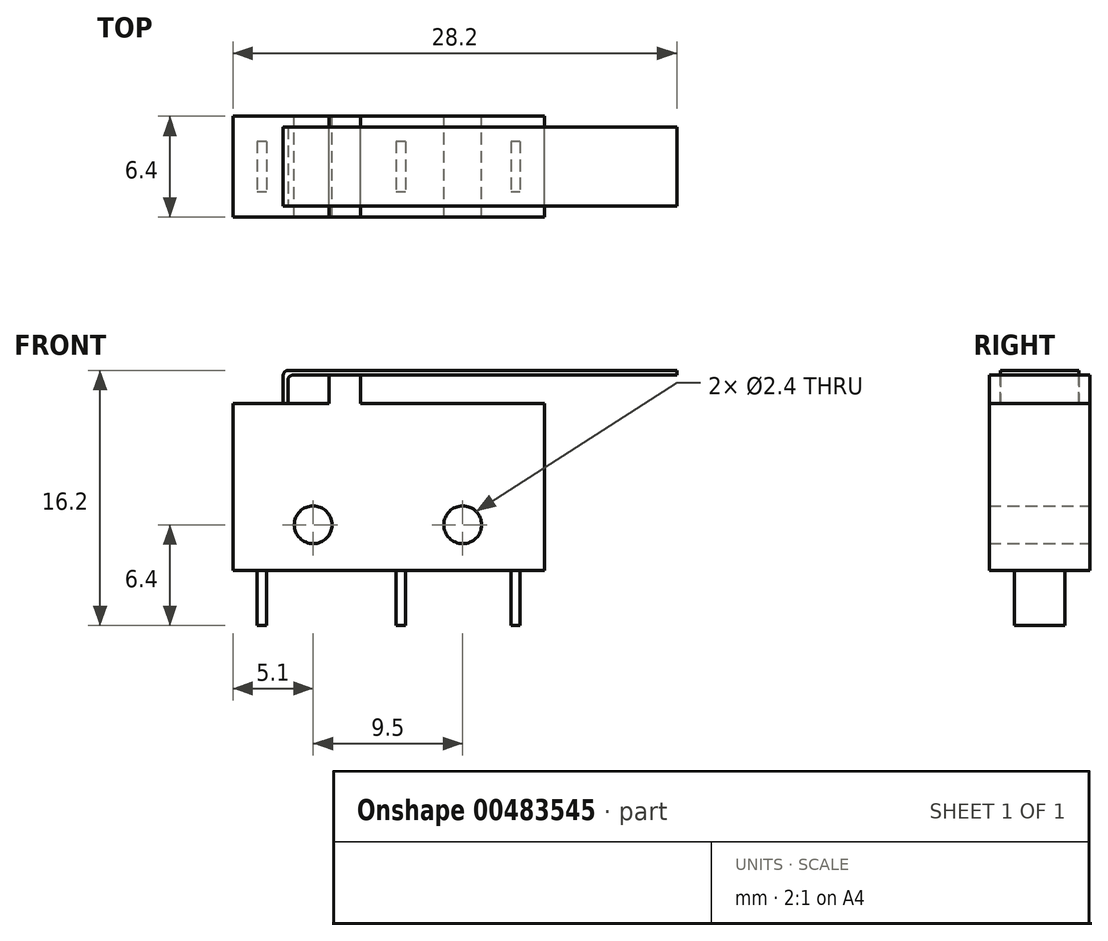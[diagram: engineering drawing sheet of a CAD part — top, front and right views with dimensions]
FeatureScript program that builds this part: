
annotation { "Feature Type Name" : "Feature", "Feature Type Description" : "" }
export const myFeature = defineFeature(function(context is Context, id is Id, definition is map)
    precondition{}
    {
        {
            var Q0;
            Q0=qCreatedBy(makeId("Front.planeOp"),FACE);
            var sketch = newSketch(context, id + "F0", { "sketchPlane" : qUnion([Q0])});
            skLineSegment(sketch, "E0.bottom", {"start": v(0, 0) * mm, "end": v(19.8, 0) * mm});
            skLineSegment(sketch, "E0.top", {"start": v(0, 10.6) * mm, "end": v(6.1, 10.6) * mm});
            skLineSegment(sketch, "E0.left", {"start": v(0, 0) * mm, "end": v(0, 10.6) * mm});
            skLineSegment(sketch, "E0.right", {"start": v(19.8, 0) * mm, "end": v(19.8, 10.6) * mm});
            skCircle(sketch, "E1", {"center": v(5.1, 2.9) * mm, "radius": 1.2 * mm});
            skCircle(sketch, "E2", {"center": v(14.6, 2.9) * mm, "radius": 1.2 * mm});
            skLineSegment(sketch, "E3", {"start": v(6.1, 10.6) * mm, "end": v(6.1, 12.4) * mm});
            skLineSegment(sketch, "E4", {"start": v(6.1, 12.4) * mm, "end": v(8.1, 12.4) * mm});
            skLineSegment(sketch, "E5", {"start": v(8.1, 12.4) * mm, "end": v(8.1, 10.6) * mm});
            skLineSegment(sketch, "E6.trimOffspring", {"start": v(8.1, 10.6) * mm, "end": v(19.8, 10.6) * mm});
            skSolve(sketch);
        }
        {
            var Q0;
            Q0 = qSketchRegion(id + "F0", true);
            extrude(context, id + "F1", {"entities" : qUnion([Q0]), "depth" : 6.4 * mm, "offsetDistance" : 25 * mm});
        }
        {
            var Q0;
            Q0=makeQuery(id+"F1.opExtrude","SWEPT_FACE",FACE,{"disambiguationData":[OSD([sQuery(id+"F0.wireOp",EDGE,"E0.bottom")])]});
            var sketch = newSketch(context, id + "F2", { "sketchPlane" : qUnion([Q0])});
            skLineSegment(sketch, "E7", {"start": v(0, 3.2) * mm, "end": v(19.8, 3.2) * mm, "construction": true});
            skLineSegment(sketch, "E8.bottom", {"start": v(2.15, 1.6) * mm, "end": v(1.55, 1.6) * mm});
            skLineSegment(sketch, "E8.top", {"start": v(2.15, 4.8) * mm, "end": v(1.55, 4.8) * mm});
            skLineSegment(sketch, "E8.left", {"start": v(2.15, 1.6) * mm, "end": v(2.15, 4.8) * mm});
            skLineSegment(sketch, "E8.right", {"start": v(1.55, 1.6) * mm, "end": v(1.55, 4.8) * mm});
            skPoint(sketch, "E8.middle", {"position": v(1.85, 3.2) * mm});
            skLineSegment(sketch, "E9.bottom", {"start": v(10.95, 1.6) * mm, "end": v(10.35, 1.6) * mm});
            skLineSegment(sketch, "E9.top", {"start": v(10.95, 4.8) * mm, "end": v(10.35, 4.8) * mm});
            skLineSegment(sketch, "E9.left", {"start": v(10.95, 1.6) * mm, "end": v(10.95, 4.8) * mm});
            skLineSegment(sketch, "E9.right", {"start": v(10.35, 1.6) * mm, "end": v(10.35, 4.8) * mm});
            skPoint(sketch, "E9.middle", {"position": v(10.65, 3.2) * mm});
            skLineSegment(sketch, "E10.bottom", {"start": v(18.25, 1.6) * mm, "end": v(17.65, 1.6) * mm});
            skLineSegment(sketch, "E10.top", {"start": v(18.25, 4.8) * mm, "end": v(17.65, 4.8) * mm});
            skLineSegment(sketch, "E10.left", {"start": v(18.25, 1.6) * mm, "end": v(18.25, 4.8) * mm});
            skLineSegment(sketch, "E10.right", {"start": v(17.65, 1.6) * mm, "end": v(17.65, 4.8) * mm});
            skPoint(sketch, "E10.middle", {"position": v(17.95, 3.2) * mm});
            skSolve(sketch);
        }
        {
            var Q0;
            Q0 = qSketchRegion(id + "F2", true);
            extrude(context, id + "F3", {"entities" : qUnion([Q0]), "depth" : 3.5 * mm, "offsetDistance" : 25 * mm});
        }
        {
            var Q0;
            Q0=makeQuery(id+"F1.opExtrude","SWEPT_FACE",FACE,{"disambiguationData":[OSD([sQuery(id+"F0.wireOp",EDGE,"E4")])]});
            var sketch = newSketch(context, id + "F4", { "sketchPlane" : qUnion([Q0])});
            skLineSegment(sketch, "E11.bottom", {"start": v(3.2, -0.7) * mm, "end": v(28.2, -0.7) * mm});
            skLineSegment(sketch, "E11.top", {"start": v(3.2, -5.7) * mm, "end": v(28.2, -5.7) * mm});
            skLineSegment(sketch, "E11.left", {"start": v(3.2, -0.7) * mm, "end": v(3.2, -5.7) * mm});
            skLineSegment(sketch, "E11.right", {"start": v(28.2, -0.7) * mm, "end": v(28.2, -5.7) * mm});
            skSolve(sketch);
        }
        {
            var Q0;
            Q0 = qSketchRegion(id + "F4", true);
            extrude(context, id + "F5", {"entities" : qUnion([Q0]), "depth" : 0.3 * mm, "offsetDistance" : 25 * mm});
        }
        {
            var Q0;
            Q0=makeQuery(id+"F5.opExtrude","CAP_FACE",FACE,{"disambiguationData":[OSD([sQuery(id+"F4.wireOp",EDGE,"E11.bottom"),sQuery(id+"F4.wireOp",EDGE,"E11.top"),sQuery(id+"F4.wireOp",EDGE,"E11.left"),sQuery(id+"F4.wireOp",EDGE,"E11.right")])],"isStart":false});
            var sketch = newSketch(context, id + "F6", { "sketchPlane" : qUnion([Q0])});
            skLineSegment(sketch, "E12.bottom", {"start": v(3.2, -0.7) * mm, "end": v(3.5, -0.7) * mm});
            skLineSegment(sketch, "E12.top", {"start": v(3.2, -5.7) * mm, "end": v(3.5, -5.7) * mm});
            skLineSegment(sketch, "E12.left", {"start": v(3.2, -0.7) * mm, "end": v(3.2, -5.7) * mm});
            skLineSegment(sketch, "E12.right", {"start": v(3.5, -0.7) * mm, "end": v(3.5, -5.7) * mm});
            skSolve(sketch);
        }
        {
            var Q0;
            Q0 = qSketchRegion(id + "F6", true);
            extrude(context, id + "F7", {"entities" : qUnion([Q0]), "operationType" : NewBodyOperationType.ADD, "oppositeDirection" : true, "depth" : 3 * mm, "offsetDistance" : 25 * mm});
        }
        {
            var Q0;
            Q0=makeQuery(id+"F5.opExtrude","CAP_EDGE",EDGE,{"disambiguationData":[OSD([sQuery(id+"F4.wireOp",EDGE,"E11.left")])],"isStart":false});
            var Q1;
            Q1=makeQuery(id+"F7.boolean.opBoolean","INTERSECT",EDGE,{"derivedFrom":[makeQuery(id+"F5.opExtrude","CAP_FACE",FACE,{"disambiguationData":[OSD([sQuery(id+"F4.wireOp",EDGE,"E11.bottom"),sQuery(id+"F4.wireOp",EDGE,"E11.top"),sQuery(id+"F4.wireOp",EDGE,"E11.left"),sQuery(id+"F4.wireOp",EDGE,"E11.right")])],"isStart":true}),makeQuery(id+"F7.opExtrude","SWEPT_FACE",FACE,{"disambiguationData":[OSD([sQuery(id+"F6.wireOp",EDGE,"E12.right")])]})]});
            fillet(context, id + "F8", {"entities" : qUnion([Q0, Q1]), "radius" : 0.3 * mm, "tangentPropagation" : true, "allowEdgeOverflow" : false});
        }
    });
